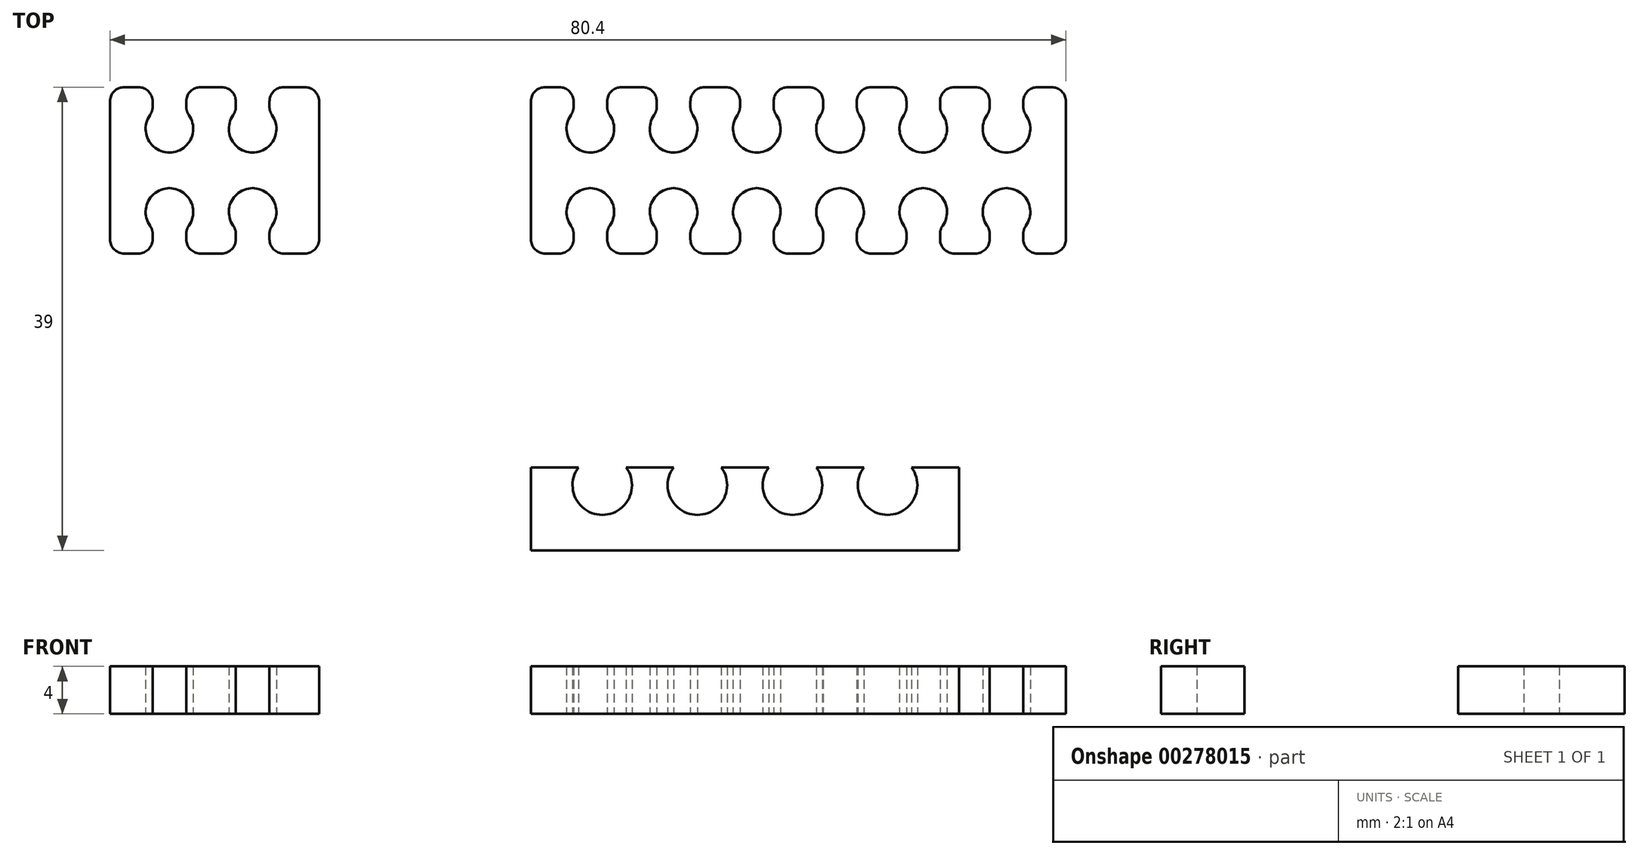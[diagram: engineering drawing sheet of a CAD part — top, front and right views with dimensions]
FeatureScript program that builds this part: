
annotation { "Feature Type Name" : "Feature", "Feature Type Description" : "" }
export const myFeature = defineFeature(function(context is Context, id is Id, definition is map)
    precondition{}
    {
        {
            var Q0;
            Q0=qCreatedBy(makeId("Top.planeOp"),FACE);
            var sketch = newSketch(context, id + "F0", { "sketchPlane" : qUnion([Q0])});
            skArc(sketch, "E0", {"start": v(4, 7) * mm, "mid": v(6, 3) * mm, "end": v(8, 7) * mm});
            skArc(sketch, "E1", {"start": v(12, 7) * mm, "mid": v(14, 3) * mm, "end": v(16, 7) * mm});
            skArc(sketch, "E2", {"start": v(20, 7) * mm, "mid": v(22, 3) * mm, "end": v(24, 7) * mm});
            skArc(sketch, "E3", {"start": v(28, 7) * mm, "mid": v(30, 3) * mm, "end": v(32, 7) * mm});
            skLineSegment(sketch, "E4", {"start": v(4, 7) * mm, "end": v(0, 7) * mm});
            skLineSegment(sketch, "E5", {"start": v(0, 7) * mm, "end": v(0, 0) * mm});
            skLineSegment(sketch, "E6", {"start": v(0, 0) * mm, "end": v(36, 0) * mm});
            skLineSegment(sketch, "E7", {"start": v(36, 0) * mm, "end": v(36, 7) * mm});
            skLineSegment(sketch, "E8", {"start": v(36, 7) * mm, "end": v(32, 7) * mm});
            skLineSegment(sketch, "E9", {"start": v(6, 5.5) * mm, "end": v(3.5, 5.5) * mm, "construction": true});
            skLineSegment(sketch, "E10", {"start": v(6, 5.5) * mm, "end": v(4, 7) * mm, "construction": true});
            skLineSegment(sketch, "E11", {"start": v(28, 7) * mm, "end": v(24, 7) * mm});
            skLineSegment(sketch, "E12", {"start": v(20, 7) * mm, "end": v(16, 7) * mm});
            skLineSegment(sketch, "E13", {"start": v(12, 7) * mm, "end": v(8, 7) * mm});
            skLineSegment(sketch, "E14", {"start": v(8.5, 5.5) * mm, "end": v(11.5, 5.5) * mm, "construction": true});
            skLineSegment(sketch, "E15", {"start": v(6, 3) * mm, "end": v(6, 0) * mm, "construction": true});
            skArc(sketch, "E16", {"start": v(3.37, 36.65) * mm, "mid": v(5, 33.5) * mm, "end": v(6.63, 36.65) * mm});
            skLineSegment(sketch, "E17", {"start": v(3.59, 37.35) * mm, "end": v(3.59, 37.8) * mm});
            skLineSegment(sketch, "E18", {"start": v(2.39, 39) * mm, "end": v(1.5, 39) * mm});
            skLineSegment(sketch, "E19", {"start": v(6.41, 37.35) * mm, "end": v(6.41, 37.8) * mm});
            skLineSegment(sketch, "E20", {"start": v(7.61, 39) * mm, "end": v(8.5, 39) * mm});
            skLineSegment(sketch, "E21", {"start": v(5, 35.5) * mm, "end": v(3, 35.5) * mm, "construction": true});
            skLineSegment(sketch, "E22", {"start": v(5, 35.5) * mm, "end": v(3.59, 36.91) * mm, "construction": true});
            skPoint(sketch, "E23.visualSharp", {"position": v(6.41, 36.91) * mm});
            skArc(sketch, "E23.filletArc", {"start": v(6.41, 37.35) * mm, "mid": v(6.47, 36.98) * mm, "end": v(6.63, 36.65) * mm});
            skPoint(sketch, "E24.visualSharp", {"position": v(6.41, 39) * mm});
            skArc(sketch, "E24.filletArc", {"start": v(7.61, 39) * mm, "mid": v(6.77, 38.65) * mm, "end": v(6.41, 37.8) * mm});
            skPoint(sketch, "E25.visualSharp", {"position": v(3.59, 39) * mm});
            skArc(sketch, "E25.filletArc", {"start": v(3.59, 37.8) * mm, "mid": v(3.23, 38.65) * mm, "end": v(2.39, 39) * mm});
            skPoint(sketch, "E26.visualSharp", {"position": v(3.59, 36.91) * mm});
            skArc(sketch, "E26.filletArc", {"start": v(3.37, 36.65) * mm, "mid": v(3.53, 36.98) * mm, "end": v(3.59, 37.35) * mm});
            skArc(sketch, "E27.1.0.0", {"start": v(10.37, 36.65) * mm, "mid": v(12, 33.5) * mm, "end": v(13.63, 36.65) * mm});
            skPoint(sketch, "E27.1.0.1", {"position": v(13.41, 36.91) * mm});
            skPoint(sketch, "E27.1.0.2", {"position": v(10.59, 36.91) * mm});
            skPoint(sketch, "E27.1.0.3", {"position": v(13.41, 39) * mm});
            skPoint(sketch, "E27.1.0.4", {"position": v(10.59, 39) * mm});
            skLineSegment(sketch, "E27.1.0.5", {"start": v(12, 35.5) * mm, "end": v(10, 35.5) * mm, "construction": true});
            skLineSegment(sketch, "E27.1.0.6", {"start": v(12, 35.5) * mm, "end": v(10.59, 36.91) * mm, "construction": true});
            skArc(sketch, "E27.1.0.7", {"start": v(10.59, 37.8) * mm, "mid": v(10.23, 38.65) * mm, "end": v(9.39, 39) * mm});
            skArc(sketch, "E27.1.0.8", {"start": v(14.61, 39) * mm, "mid": v(13.77, 38.65) * mm, "end": v(13.41, 37.8) * mm});
            skLineSegment(sketch, "E27.1.0.9", {"start": v(9.39, 39) * mm, "end": v(8.5, 39) * mm});
            skLineSegment(sketch, "E27.1.0.10", {"start": v(14.61, 39) * mm, "end": v(15.5, 39) * mm});
            skLineSegment(sketch, "E27.1.0.11", {"start": v(10.59, 37.35) * mm, "end": v(10.59, 37.8) * mm});
            skLineSegment(sketch, "E27.1.0.12", {"start": v(13.41, 37.35) * mm, "end": v(13.41, 37.8) * mm});
            skArc(sketch, "E27.1.0.13", {"start": v(10.37, 36.65) * mm, "mid": v(10.53, 36.98) * mm, "end": v(10.59, 37.35) * mm});
            skArc(sketch, "E27.1.0.14", {"start": v(13.41, 37.35) * mm, "mid": v(13.47, 36.98) * mm, "end": v(13.63, 36.65) * mm});
            skArc(sketch, "E27.2.0.0", {"start": v(17.37, 36.65) * mm, "mid": v(19, 33.5) * mm, "end": v(20.63, 36.65) * mm});
            skPoint(sketch, "E27.2.0.1", {"position": v(20.41, 36.91) * mm});
            skPoint(sketch, "E27.2.0.2", {"position": v(17.59, 36.91) * mm});
            skPoint(sketch, "E27.2.0.3", {"position": v(20.41, 39) * mm});
            skPoint(sketch, "E27.2.0.4", {"position": v(17.59, 39) * mm});
            skLineSegment(sketch, "E27.2.0.5", {"start": v(19, 35.5) * mm, "end": v(17, 35.5) * mm, "construction": true});
            skLineSegment(sketch, "E27.2.0.6", {"start": v(19, 35.5) * mm, "end": v(17.59, 36.91) * mm, "construction": true});
            skArc(sketch, "E27.2.0.7", {"start": v(17.59, 37.8) * mm, "mid": v(17.23, 38.65) * mm, "end": v(16.39, 39) * mm});
            skArc(sketch, "E27.2.0.8", {"start": v(21.61, 39) * mm, "mid": v(20.77, 38.65) * mm, "end": v(20.41, 37.8) * mm});
            skLineSegment(sketch, "E27.2.0.9", {"start": v(16.39, 39) * mm, "end": v(15.5, 39) * mm});
            skLineSegment(sketch, "E27.2.0.10", {"start": v(21.61, 39) * mm, "end": v(22.5, 39) * mm});
            skLineSegment(sketch, "E27.2.0.11", {"start": v(17.59, 37.35) * mm, "end": v(17.59, 37.8) * mm});
            skLineSegment(sketch, "E27.2.0.12", {"start": v(20.41, 37.35) * mm, "end": v(20.41, 37.8) * mm});
            skArc(sketch, "E27.2.0.13", {"start": v(17.37, 36.65) * mm, "mid": v(17.53, 36.98) * mm, "end": v(17.59, 37.35) * mm});
            skArc(sketch, "E27.2.0.14", {"start": v(20.41, 37.35) * mm, "mid": v(20.47, 36.98) * mm, "end": v(20.63, 36.65) * mm});
            skArc(sketch, "E27.3.0.0", {"start": v(24.37, 36.65) * mm, "mid": v(26, 33.5) * mm, "end": v(27.63, 36.65) * mm});
            skPoint(sketch, "E27.3.0.1", {"position": v(27.41, 36.91) * mm});
            skPoint(sketch, "E27.3.0.2", {"position": v(24.59, 36.91) * mm});
            skPoint(sketch, "E27.3.0.3", {"position": v(27.41, 39) * mm});
            skPoint(sketch, "E27.3.0.4", {"position": v(24.59, 39) * mm});
            skLineSegment(sketch, "E27.3.0.5", {"start": v(26, 35.5) * mm, "end": v(24, 35.5) * mm, "construction": true});
            skLineSegment(sketch, "E27.3.0.6", {"start": v(26, 35.5) * mm, "end": v(24.59, 36.91) * mm, "construction": true});
            skArc(sketch, "E27.3.0.7", {"start": v(24.59, 37.8) * mm, "mid": v(24.23, 38.65) * mm, "end": v(23.39, 39) * mm});
            skArc(sketch, "E27.3.0.8", {"start": v(28.61, 39) * mm, "mid": v(27.77, 38.65) * mm, "end": v(27.41, 37.8) * mm});
            skLineSegment(sketch, "E27.3.0.9", {"start": v(23.39, 39) * mm, "end": v(22.5, 39) * mm});
            skLineSegment(sketch, "E27.3.0.10", {"start": v(28.61, 39) * mm, "end": v(29.5, 39) * mm});
            skLineSegment(sketch, "E27.3.0.11", {"start": v(24.59, 37.35) * mm, "end": v(24.59, 37.8) * mm});
            skLineSegment(sketch, "E27.3.0.12", {"start": v(27.41, 37.35) * mm, "end": v(27.41, 37.8) * mm});
            skArc(sketch, "E27.3.0.13", {"start": v(24.37, 36.65) * mm, "mid": v(24.53, 36.98) * mm, "end": v(24.59, 37.35) * mm});
            skArc(sketch, "E27.3.0.14", {"start": v(27.41, 37.35) * mm, "mid": v(27.47, 36.98) * mm, "end": v(27.63, 36.65) * mm});
            skArc(sketch, "E27.4.0.0", {"start": v(31.37, 36.65) * mm, "mid": v(33, 33.5) * mm, "end": v(34.63, 36.65) * mm});
            skPoint(sketch, "E27.4.0.1", {"position": v(34.41, 36.91) * mm});
            skPoint(sketch, "E27.4.0.2", {"position": v(31.59, 36.91) * mm});
            skPoint(sketch, "E27.4.0.3", {"position": v(34.41, 39) * mm});
            skPoint(sketch, "E27.4.0.4", {"position": v(31.59, 39) * mm});
            skLineSegment(sketch, "E27.4.0.5", {"start": v(33, 35.5) * mm, "end": v(31, 35.5) * mm, "construction": true});
            skLineSegment(sketch, "E27.4.0.6", {"start": v(33, 35.5) * mm, "end": v(31.59, 36.91) * mm, "construction": true});
            skArc(sketch, "E27.4.0.7", {"start": v(31.59, 37.8) * mm, "mid": v(31.23, 38.65) * mm, "end": v(30.39, 39) * mm});
            skArc(sketch, "E27.4.0.8", {"start": v(35.61, 39) * mm, "mid": v(34.77, 38.65) * mm, "end": v(34.41, 37.8) * mm});
            skLineSegment(sketch, "E27.4.0.9", {"start": v(30.39, 39) * mm, "end": v(29.5, 39) * mm});
            skLineSegment(sketch, "E27.4.0.10", {"start": v(35.61, 39) * mm, "end": v(36.5, 39) * mm});
            skLineSegment(sketch, "E27.4.0.11", {"start": v(31.59, 37.35) * mm, "end": v(31.59, 37.8) * mm});
            skLineSegment(sketch, "E27.4.0.12", {"start": v(34.41, 37.35) * mm, "end": v(34.41, 37.8) * mm});
            skArc(sketch, "E27.4.0.13", {"start": v(31.37, 36.65) * mm, "mid": v(31.53, 36.98) * mm, "end": v(31.59, 37.35) * mm});
            skArc(sketch, "E27.4.0.14", {"start": v(34.41, 37.35) * mm, "mid": v(34.47, 36.98) * mm, "end": v(34.63, 36.65) * mm});
            skArc(sketch, "E27.5.0.0", {"start": v(38.37, 36.65) * mm, "mid": v(40, 33.5) * mm, "end": v(41.63, 36.65) * mm});
            skPoint(sketch, "E27.5.0.1", {"position": v(41.41, 36.91) * mm});
            skPoint(sketch, "E27.5.0.2", {"position": v(38.59, 36.91) * mm});
            skPoint(sketch, "E27.5.0.3", {"position": v(41.41, 39) * mm});
            skPoint(sketch, "E27.5.0.4", {"position": v(38.59, 39) * mm});
            skLineSegment(sketch, "E27.5.0.5", {"start": v(40, 35.5) * mm, "end": v(38, 35.5) * mm, "construction": true});
            skLineSegment(sketch, "E27.5.0.6", {"start": v(40, 35.5) * mm, "end": v(38.59, 36.91) * mm, "construction": true});
            skArc(sketch, "E27.5.0.7", {"start": v(38.59, 37.8) * mm, "mid": v(38.23, 38.65) * mm, "end": v(37.39, 39) * mm});
            skArc(sketch, "E27.5.0.8", {"start": v(42.61, 39) * mm, "mid": v(41.77, 38.65) * mm, "end": v(41.41, 37.8) * mm});
            skLineSegment(sketch, "E27.5.0.9", {"start": v(37.39, 39) * mm, "end": v(36.5, 39) * mm});
            skLineSegment(sketch, "E27.5.0.10", {"start": v(42.61, 39) * mm, "end": v(43.5, 39) * mm});
            skLineSegment(sketch, "E27.5.0.11", {"start": v(38.59, 37.35) * mm, "end": v(38.59, 37.8) * mm});
            skLineSegment(sketch, "E27.5.0.12", {"start": v(41.41, 37.35) * mm, "end": v(41.41, 37.8) * mm});
            skArc(sketch, "E27.5.0.13", {"start": v(38.37, 36.65) * mm, "mid": v(38.53, 36.98) * mm, "end": v(38.59, 37.35) * mm});
            skArc(sketch, "E27.5.0.14", {"start": v(41.41, 37.35) * mm, "mid": v(41.47, 36.98) * mm, "end": v(41.63, 36.65) * mm});
            skLineSegment(sketch, "E27.direction1", {"start": v(3, 35.5) * mm, "end": v(10, 35.5) * mm, "construction": true});
            skLineSegment(sketch, "E28", {"start": v(5, 32) * mm, "end": v(12, 32) * mm, "construction": true});
            skPoint(sketch, "E29", {"position": v(5, 33.5) * mm});
            skPoint(sketch, "E30", {"position": v(7, 35.5) * mm});
            skPoint(sketch, "E31", {"position": v(10, 35.5) * mm});
            skLineSegment(sketch, "E32.MirrorCS", {"start": v(24.59, 26.65) * mm, "end": v(24.59, 26.2) * mm});
            skLineSegment(sketch, "E33.MirrorCS", {"start": v(10.59, 26.65) * mm, "end": v(10.59, 26.2) * mm});
            skLineSegment(sketch, "E34.MirrorCS", {"start": v(27.41, 26.65) * mm, "end": v(27.41, 26.2) * mm});
            skArc(sketch, "E35.MirrorCS", {"start": v(41.41, 26.65) * mm, "mid": v(41.47, 27.02) * mm, "end": v(41.63, 27.35) * mm});
            skLineSegment(sketch, "E36.MirrorCS", {"start": v(3.59, 26.65) * mm, "end": v(3.59, 26.2) * mm});
            skArc(sketch, "E37.MirrorCS", {"start": v(20.41, 26.65) * mm, "mid": v(20.47, 27.02) * mm, "end": v(20.63, 27.35) * mm});
            skArc(sketch, "E38.MirrorCS", {"start": v(38.37, 27.35) * mm, "mid": v(38.53, 27.02) * mm, "end": v(38.59, 26.65) * mm});
            skArc(sketch, "E39.MirrorCS", {"start": v(6.41, 26.65) * mm, "mid": v(6.47, 27.02) * mm, "end": v(6.63, 27.35) * mm});
            skArc(sketch, "E40.MirrorCS", {"start": v(17.37, 27.35) * mm, "mid": v(17.53, 27.02) * mm, "end": v(17.59, 26.65) * mm});
            skArc(sketch, "E41.MirrorCS", {"start": v(34.41, 26.65) * mm, "mid": v(34.47, 27.02) * mm, "end": v(34.63, 27.35) * mm});
            skLineSegment(sketch, "E42.MirrorCS", {"start": v(41.41, 26.65) * mm, "end": v(41.41, 26.2) * mm});
            skArc(sketch, "E43.MirrorCS", {"start": v(3.37, 27.35) * mm, "mid": v(3.53, 27.02) * mm, "end": v(3.59, 26.65) * mm});
            skLineSegment(sketch, "E44.MirrorCS", {"start": v(34.41, 26.65) * mm, "end": v(34.41, 26.2) * mm});
            skArc(sketch, "E45.MirrorCS", {"start": v(27.41, 26.65) * mm, "mid": v(27.47, 27.02) * mm, "end": v(27.63, 27.35) * mm});
            skArc(sketch, "E46.MirrorCS", {"start": v(24.37, 27.35) * mm, "mid": v(24.53, 27.02) * mm, "end": v(24.59, 26.65) * mm});
            skLineSegment(sketch, "E47.MirrorCS", {"start": v(13.41, 26.65) * mm, "end": v(13.41, 26.2) * mm});
            skLineSegment(sketch, "E48.MirrorCS", {"start": v(38.59, 26.65) * mm, "end": v(38.59, 26.2) * mm});
            skLineSegment(sketch, "E49.MirrorCS", {"start": v(31.59, 26.65) * mm, "end": v(31.59, 26.2) * mm});
            skLineSegment(sketch, "E50.MirrorCS", {"start": v(6.41, 26.65) * mm, "end": v(6.41, 26.2) * mm});
            skLineSegment(sketch, "E51.MirrorCS", {"start": v(17.59, 26.65) * mm, "end": v(17.59, 26.2) * mm});
            skArc(sketch, "E52.MirrorCS", {"start": v(13.41, 26.65) * mm, "mid": v(13.47, 27.02) * mm, "end": v(13.63, 27.35) * mm});
            skLineSegment(sketch, "E53.MirrorCS", {"start": v(20.41, 26.65) * mm, "end": v(20.41, 26.2) * mm});
            skArc(sketch, "E54.MirrorCS", {"start": v(31.37, 27.35) * mm, "mid": v(31.53, 27.02) * mm, "end": v(31.59, 26.65) * mm});
            skArc(sketch, "E55.MirrorCS", {"start": v(10.37, 27.35) * mm, "mid": v(10.53, 27.02) * mm, "end": v(10.59, 26.65) * mm});
            skLineSegment(sketch, "E56.MirrorCS", {"start": v(35.61, 25) * mm, "end": v(36.5, 25) * mm});
            skLineSegment(sketch, "E57.MirrorCS", {"start": v(14.61, 25) * mm, "end": v(15.5, 25) * mm});
            skLineSegment(sketch, "E58.MirrorCS", {"start": v(30.39, 25) * mm, "end": v(29.5, 25) * mm});
            skLineSegment(sketch, "E59.MirrorCS", {"start": v(9.39, 25) * mm, "end": v(8.5, 25) * mm});
            skLineSegment(sketch, "E60.MirrorCS", {"start": v(28.61, 25) * mm, "end": v(29.5, 25) * mm});
            skLineSegment(sketch, "E61.MirrorCS", {"start": v(23.39, 25) * mm, "end": v(22.5, 25) * mm});
            skLineSegment(sketch, "E62.MirrorCS", {"start": v(16.39, 25) * mm, "end": v(15.5, 25) * mm});
            skLineSegment(sketch, "E63.MirrorCS", {"start": v(7.61, 25) * mm, "end": v(8.5, 25) * mm});
            skLineSegment(sketch, "E64.MirrorCS", {"start": v(37.39, 25) * mm, "end": v(36.5, 25) * mm});
            skLineSegment(sketch, "E65.MirrorCS", {"start": v(21.61, 25) * mm, "end": v(22.5, 25) * mm});
            skLineSegment(sketch, "E66.MirrorCS", {"start": v(2.39, 25) * mm, "end": v(1.5, 25) * mm});
            skArc(sketch, "E67.MirrorCS", {"start": v(17.59, 26.2) * mm, "mid": v(17.23, 25.35) * mm, "end": v(16.39, 25) * mm});
            skArc(sketch, "E68.MirrorCS", {"start": v(3.59, 26.2) * mm, "mid": v(3.23, 25.35) * mm, "end": v(2.39, 25) * mm});
            skArc(sketch, "E69.MirrorCS", {"start": v(7.61, 25) * mm, "mid": v(6.77, 25.35) * mm, "end": v(6.41, 26.2) * mm});
            skArc(sketch, "E70.MirrorCS", {"start": v(35.61, 25) * mm, "mid": v(34.77, 25.35) * mm, "end": v(34.41, 26.2) * mm});
            skArc(sketch, "E71.MirrorCS", {"start": v(14.61, 25) * mm, "mid": v(13.77, 25.35) * mm, "end": v(13.41, 26.2) * mm});
            skArc(sketch, "E72.MirrorCS", {"start": v(31.59, 26.2) * mm, "mid": v(31.23, 25.35) * mm, "end": v(30.39, 25) * mm});
            skArc(sketch, "E73.MirrorCS", {"start": v(21.61, 25) * mm, "mid": v(20.77, 25.35) * mm, "end": v(20.41, 26.2) * mm});
            skArc(sketch, "E74.MirrorCS", {"start": v(38.59, 26.2) * mm, "mid": v(38.23, 25.35) * mm, "end": v(37.39, 25) * mm});
            skArc(sketch, "E75.MirrorCS", {"start": v(42.61, 25) * mm, "mid": v(41.77, 25.35) * mm, "end": v(41.41, 26.2) * mm});
            skLineSegment(sketch, "E76.MirrorCS", {"start": v(42.61, 25) * mm, "end": v(43.5, 25) * mm});
            skLineSegment(sketch, "E77.MirrorCS", {"start": v(5, 28.5) * mm, "end": v(3, 28.5) * mm, "construction": true});
            skArc(sketch, "E78.MirrorCS", {"start": v(24.59, 26.2) * mm, "mid": v(24.23, 25.35) * mm, "end": v(23.39, 25) * mm});
            skArc(sketch, "E79.MirrorCS", {"start": v(10.59, 26.2) * mm, "mid": v(10.23, 25.35) * mm, "end": v(9.39, 25) * mm});
            skArc(sketch, "E80.MirrorCS", {"start": v(28.61, 25) * mm, "mid": v(27.77, 25.35) * mm, "end": v(27.41, 26.2) * mm});
            skPoint(sketch, "E81.MirrorP", {"position": v(10.59, 25) * mm});
            skPoint(sketch, "E82.MirrorP", {"position": v(24.59, 27.09) * mm});
            skLineSegment(sketch, "E83.MirrorCS", {"start": v(26, 28.5) * mm, "end": v(24, 28.5) * mm, "construction": true});
            skLineSegment(sketch, "E84.MirrorCS", {"start": v(3, 28.5) * mm, "end": v(10, 28.5) * mm, "construction": true});
            skPoint(sketch, "E85.MirrorP", {"position": v(31.59, 27.09) * mm});
            skPoint(sketch, "E86.MirrorP", {"position": v(5, 30.5) * mm});
            skLineSegment(sketch, "E87.MirrorCS", {"start": v(40, 28.5) * mm, "end": v(38.59, 27.09) * mm, "construction": true});
            skPoint(sketch, "E88.MirrorP", {"position": v(17.59, 25) * mm});
            skArc(sketch, "E89.MirrorCS", {"start": v(24.37, 27.35) * mm, "mid": v(26, 30.5) * mm, "end": v(27.63, 27.35) * mm});
            skPoint(sketch, "E90.MirrorP", {"position": v(34.41, 27.09) * mm});
            skPoint(sketch, "E91.MirrorP", {"position": v(3.59, 25) * mm});
            skPoint(sketch, "E92.MirrorP", {"position": v(20.41, 25) * mm});
            skLineSegment(sketch, "E93.MirrorCS", {"start": v(40, 28.5) * mm, "end": v(38, 28.5) * mm, "construction": true});
            skLineSegment(sketch, "E94.MirrorCS", {"start": v(19, 28.5) * mm, "end": v(17.59, 27.09) * mm, "construction": true});
            skPoint(sketch, "E95.MirrorP", {"position": v(13.41, 25) * mm});
            skPoint(sketch, "E96.MirrorP", {"position": v(27.41, 27.09) * mm});
            skArc(sketch, "E97.MirrorCS", {"start": v(3.37, 27.35) * mm, "mid": v(5, 30.5) * mm, "end": v(6.63, 27.35) * mm});
            skPoint(sketch, "E98.MirrorP", {"position": v(17.59, 27.09) * mm});
            skArc(sketch, "E99.MirrorCS", {"start": v(38.37, 27.35) * mm, "mid": v(40, 30.5) * mm, "end": v(41.63, 27.35) * mm});
            skLineSegment(sketch, "E100.MirrorCS", {"start": v(19, 28.5) * mm, "end": v(17, 28.5) * mm, "construction": true});
            skPoint(sketch, "E101.MirrorP", {"position": v(10.59, 27.09) * mm});
            skArc(sketch, "E102.MirrorCS", {"start": v(17.37, 27.35) * mm, "mid": v(19, 30.5) * mm, "end": v(20.63, 27.35) * mm});
            skLineSegment(sketch, "E103.MirrorCS", {"start": v(5, 28.5) * mm, "end": v(3.59, 27.09) * mm, "construction": true});
            skPoint(sketch, "E104.MirrorP", {"position": v(6.41, 25) * mm});
            skPoint(sketch, "E105.MirrorP", {"position": v(13.41, 27.09) * mm});
            skPoint(sketch, "E106.MirrorP", {"position": v(20.41, 27.09) * mm});
            skPoint(sketch, "E107.MirrorP", {"position": v(24.59, 25) * mm});
            skPoint(sketch, "E108.MirrorP", {"position": v(6.41, 27.09) * mm});
            skPoint(sketch, "E109.MirrorP", {"position": v(7, 28.5) * mm});
            skPoint(sketch, "E110.MirrorP", {"position": v(27.41, 25) * mm});
            skPoint(sketch, "E111.MirrorP", {"position": v(41.41, 27.09) * mm});
            skPoint(sketch, "E112.MirrorP", {"position": v(31.59, 25) * mm});
            skLineSegment(sketch, "E113.MirrorCS", {"start": v(26, 28.5) * mm, "end": v(24.59, 27.09) * mm, "construction": true});
            skPoint(sketch, "E114.MirrorP", {"position": v(10, 28.5) * mm});
            skPoint(sketch, "E115.MirrorP", {"position": v(38.59, 25) * mm});
            skArc(sketch, "E116.MirrorCS", {"start": v(10.37, 27.35) * mm, "mid": v(12, 30.5) * mm, "end": v(13.63, 27.35) * mm});
            skPoint(sketch, "E117.MirrorP", {"position": v(34.41, 25) * mm});
            skPoint(sketch, "E118.MirrorP", {"position": v(3.59, 27.09) * mm});
            skPoint(sketch, "E119.MirrorP", {"position": v(38.59, 27.09) * mm});
            skPoint(sketch, "E120.MirrorP", {"position": v(41.41, 25) * mm});
            skLineSegment(sketch, "E121.MirrorCS", {"start": v(33, 28.5) * mm, "end": v(31, 28.5) * mm, "construction": true});
            skLineSegment(sketch, "E122.MirrorCS", {"start": v(33, 28.5) * mm, "end": v(31.59, 27.09) * mm, "construction": true});
            skLineSegment(sketch, "E123.MirrorCS", {"start": v(12, 28.5) * mm, "end": v(10.59, 27.09) * mm, "construction": true});
            skLineSegment(sketch, "E124.MirrorCS", {"start": v(12, 28.5) * mm, "end": v(10, 28.5) * mm, "construction": true});
            skArc(sketch, "E125.MirrorCS", {"start": v(31.37, 27.35) * mm, "mid": v(33, 30.5) * mm, "end": v(34.63, 27.35) * mm});
            skLineSegment(sketch, "E126", {"start": v(1.5, 39) * mm, "end": v(1.2, 39) * mm});
            skLineSegment(sketch, "E127", {"start": v(0, 37.8) * mm, "end": v(0, 26.2) * mm});
            skLineSegment(sketch, "E128", {"start": v(1.2, 25) * mm, "end": v(1.5, 25) * mm});
            skLineSegment(sketch, "E129", {"start": v(43.5, 25) * mm, "end": v(43.8, 25) * mm});
            skLineSegment(sketch, "E130", {"start": v(45, 26.2) * mm, "end": v(45, 37.8) * mm});
            skLineSegment(sketch, "E131", {"start": v(43.8, 39) * mm, "end": v(43.5, 39) * mm});
            skPoint(sketch, "E132.visualSharp", {"position": v(0, 39) * mm});
            skArc(sketch, "E132.filletArc", {"start": v(1.2, 39) * mm, "mid": v(0.35, 38.65) * mm, "end": v(0, 37.8) * mm});
            skPoint(sketch, "E133.visualSharp", {"position": v(0, 25) * mm});
            skArc(sketch, "E133.filletArc", {"start": v(0, 26.2) * mm, "mid": v(0.35, 25.35) * mm, "end": v(1.2, 25) * mm});
            skPoint(sketch, "E134.visualSharp", {"position": v(45, 25) * mm});
            skArc(sketch, "E134.filletArc", {"start": v(43.8, 25) * mm, "mid": v(44.65, 25.35) * mm, "end": v(45, 26.2) * mm});
            skPoint(sketch, "E135.visualSharp", {"position": v(45, 39) * mm});
            skArc(sketch, "E135.filletArc", {"start": v(45, 37.8) * mm, "mid": v(44.65, 38.65) * mm, "end": v(43.8, 39) * mm});
            skLineSegment(sketch, "E136.1.0.0", {"start": v(-32.4, 35.5) * mm, "end": v(-25.4, 35.5) * mm, "construction": true});
            skPoint(sketch, "E136.1.0.1", {"position": v(-21.99, 39) * mm});
            skLineSegment(sketch, "E136.1.0.2", {"start": v(-23.4, 35.5) * mm, "end": v(-24.82, 36.91) * mm, "construction": true});
            skPoint(sketch, "E136.1.0.3", {"position": v(-31.82, 36.91) * mm});
            skPoint(sketch, "E136.1.0.4", {"position": v(-28.4, 35.5) * mm});
            skArc(sketch, "E136.1.0.5", {"start": v(-32.04, 27.35) * mm, "mid": v(-30.4, 30.5) * mm, "end": v(-28.77, 27.35) * mm});
            skLineSegment(sketch, "E136.1.0.6", {"start": v(-30.4, 28.5) * mm, "end": v(-32.4, 28.5) * mm, "construction": true});
            skArc(sketch, "E136.1.0.7", {"start": v(-25.04, 27.35) * mm, "mid": v(-23.4, 30.5) * mm, "end": v(-21.77, 27.35) * mm});
            skArc(sketch, "E136.1.0.8", {"start": v(-25.04, 36.65) * mm, "mid": v(-23.4, 33.5) * mm, "end": v(-21.77, 36.65) * mm});
            skPoint(sketch, "E136.1.0.9", {"position": v(-28.99, 27.09) * mm});
            skPoint(sketch, "E136.1.0.10", {"position": v(-24.82, 36.91) * mm});
            skPoint(sketch, "E136.1.0.11", {"position": v(-17.82, 25) * mm});
            skPoint(sketch, "E136.1.0.12", {"position": v(-35.4, 25) * mm});
            skPoint(sketch, "E136.1.0.13", {"position": v(-30.4, 30.5) * mm});
            skPoint(sketch, "E136.1.0.15", {"position": v(-25.4, 28.5) * mm});
            skArc(sketch, "E136.1.0.16", {"start": v(-32.04, 36.65) * mm, "mid": v(-30.4, 33.5) * mm, "end": v(-28.77, 36.65) * mm});
            skPoint(sketch, "E136.1.0.17", {"position": v(-21.99, 25) * mm});
            skPoint(sketch, "E136.1.0.18", {"position": v(-21.99, 36.91) * mm});
            skPoint(sketch, "E136.1.0.19", {"position": v(-28.99, 39) * mm});
            skLineSegment(sketch, "E136.1.0.20", {"start": v(-35.4, 37.8) * mm, "end": v(-35.4, 26.2) * mm});
            skPoint(sketch, "E136.1.0.21", {"position": v(-21.99, 27.09) * mm});
            skPoint(sketch, "E136.1.0.22", {"position": v(-35.4, 39) * mm});
            skPoint(sketch, "E136.1.0.23", {"position": v(-28.99, 25) * mm});
            skPoint(sketch, "E136.1.0.24", {"position": v(-24.82, 25) * mm});
            skPoint(sketch, "E136.1.0.25", {"position": v(-28.99, 36.91) * mm});
            skLineSegment(sketch, "E136.1.0.26", {"start": v(-32.4, 28.5) * mm, "end": v(-25.4, 28.5) * mm, "construction": true});
            skLineSegment(sketch, "E136.1.0.27", {"start": v(-30.4, 35.5) * mm, "end": v(-31.82, 36.91) * mm, "construction": true});
            skLineSegment(sketch, "E136.1.0.28", {"start": v(-23.4, 28.5) * mm, "end": v(-25.4, 28.5) * mm, "construction": true});
            skLineSegment(sketch, "E136.1.0.29", {"start": v(-30.4, 28.5) * mm, "end": v(-31.82, 27.09) * mm, "construction": true});
            skPoint(sketch, "E136.1.0.30", {"position": v(-24.82, 27.09) * mm});
            skPoint(sketch, "E136.1.0.31", {"position": v(-30.4, 33.5) * mm});
            skLineSegment(sketch, "E136.1.0.32", {"start": v(-23.4, 28.5) * mm, "end": v(-24.82, 27.09) * mm, "construction": true});
            skPoint(sketch, "E136.1.0.33", {"position": v(-31.82, 27.09) * mm});
            skPoint(sketch, "E136.1.0.34", {"position": v(-17.82, 39) * mm});
            skPoint(sketch, "E136.1.0.35", {"position": v(-31.82, 25) * mm});
            skLineSegment(sketch, "E136.1.0.36", {"start": v(-30.4, 32) * mm, "end": v(-23.4, 32) * mm, "construction": true});
            skLineSegment(sketch, "E136.1.0.37", {"start": v(-23.4, 35.5) * mm, "end": v(-25.4, 35.5) * mm, "construction": true});
            skPoint(sketch, "E136.1.0.38", {"position": v(-28.4, 28.5) * mm});
            skPoint(sketch, "E136.1.0.39", {"position": v(-25.4, 35.5) * mm});
            skPoint(sketch, "E136.1.0.41", {"position": v(-24.82, 39) * mm});
            skPoint(sketch, "E136.1.0.42", {"position": v(-31.82, 39) * mm});
            skArc(sketch, "E136.1.0.43", {"start": v(-34.2, 39) * mm, "mid": v(-35.05, 38.65) * mm, "end": v(-35.4, 37.8) * mm});
            skArc(sketch, "E136.1.0.44", {"start": v(-20.79, 25) * mm, "mid": v(-21.64, 25.35) * mm, "end": v(-21.99, 26.2) * mm});
            skArc(sketch, "E136.1.0.45", {"start": v(-27.79, 25) * mm, "mid": v(-28.64, 25.35) * mm, "end": v(-28.99, 26.2) * mm});
            skArc(sketch, "E136.1.0.46", {"start": v(-31.82, 37.8) * mm, "mid": v(-32.17, 38.65) * mm, "end": v(-33.02, 39) * mm});
            skArc(sketch, "E136.1.0.47", {"start": v(-17.82, 37.8) * mm, "mid": v(-18.17, 38.65) * mm, "end": v(-19.02, 39) * mm});
            skArc(sketch, "E136.1.0.48", {"start": v(-31.82, 26.2) * mm, "mid": v(-32.17, 25.35) * mm, "end": v(-33.02, 25) * mm});
            skArc(sketch, "E136.1.0.49", {"start": v(-27.79, 39) * mm, "mid": v(-28.64, 38.65) * mm, "end": v(-28.99, 37.8) * mm});
            skArc(sketch, "E136.1.0.50", {"start": v(-17.82, 26.2) * mm, "mid": v(-18.17, 25.35) * mm, "end": v(-19.02, 25) * mm});
            skArc(sketch, "E136.1.0.51", {"start": v(-20.79, 39) * mm, "mid": v(-21.64, 38.65) * mm, "end": v(-21.99, 37.8) * mm});
            skLineSegment(sketch, "E136.1.0.52", {"start": v(-30.4, 35.5) * mm, "end": v(-32.4, 35.5) * mm, "construction": true});
            skArc(sketch, "E136.1.0.53", {"start": v(-35.4, 26.2) * mm, "mid": v(-35.05, 25.35) * mm, "end": v(-34.2, 25) * mm});
            skArc(sketch, "E136.1.0.54", {"start": v(-24.82, 37.8) * mm, "mid": v(-25.17, 38.65) * mm, "end": v(-26.02, 39) * mm});
            skArc(sketch, "E136.1.0.55", {"start": v(-24.82, 26.2) * mm, "mid": v(-25.17, 25.35) * mm, "end": v(-26.02, 25) * mm});
            skLineSegment(sketch, "E136.1.0.56", {"start": v(-19.02, 25) * mm, "end": v(-19.9, 25) * mm});
            skLineSegment(sketch, "E136.1.0.57", {"start": v(-33.02, 39) * mm, "end": v(-33.9, 39) * mm});
            skLineSegment(sketch, "E136.1.0.58", {"start": v(-20.79, 25) * mm, "end": v(-19.9, 25) * mm});
            skArc(sketch, "E136.1.0.59", {"start": v(-28.99, 26.65) * mm, "mid": v(-28.93, 27.02) * mm, "end": v(-28.77, 27.35) * mm});
            skLineSegment(sketch, "E136.1.0.60", {"start": v(-20.79, 39) * mm, "end": v(-19.9, 39) * mm});
            skArc(sketch, "E136.1.0.61", {"start": v(-25.04, 27.35) * mm, "mid": v(-24.87, 27.02) * mm, "end": v(-24.82, 26.65) * mm});
            skLineSegment(sketch, "E136.1.0.62", {"start": v(-19.02, 39) * mm, "end": v(-19.9, 39) * mm});
            skLineSegment(sketch, "E136.1.0.63", {"start": v(-31.82, 37.35) * mm, "end": v(-31.82, 37.8) * mm});
            skArc(sketch, "E136.1.0.64", {"start": v(-32.04, 36.65) * mm, "mid": v(-31.87, 36.98) * mm, "end": v(-31.82, 37.35) * mm});
            skLineSegment(sketch, "E136.1.0.65", {"start": v(-26.02, 39) * mm, "end": v(-26.9, 39) * mm});
            skLineSegment(sketch, "E136.1.0.66", {"start": v(-34.2, 25) * mm, "end": v(-33.9, 25) * mm});
            skArc(sketch, "E136.1.0.67", {"start": v(-21.99, 26.65) * mm, "mid": v(-21.93, 27.02) * mm, "end": v(-21.77, 27.35) * mm});
            skLineSegment(sketch, "E136.1.0.68", {"start": v(-31.82, 26.65) * mm, "end": v(-31.82, 26.2) * mm});
            skLineSegment(sketch, "E136.1.0.69", {"start": v(-33.9, 39) * mm, "end": v(-34.2, 39) * mm});
            skArc(sketch, "E136.1.0.71", {"start": v(-28.99, 37.35) * mm, "mid": v(-28.93, 36.98) * mm, "end": v(-28.77, 36.65) * mm});
            skLineSegment(sketch, "E136.1.0.72", {"start": v(-28.99, 26.65) * mm, "end": v(-28.99, 26.2) * mm});
            skLineSegment(sketch, "E136.1.0.73", {"start": v(-26.02, 25) * mm, "end": v(-26.9, 25) * mm});
            skLineSegment(sketch, "E136.1.0.74", {"start": v(-33.02, 25) * mm, "end": v(-33.9, 25) * mm});
            skArc(sketch, "E136.1.0.75", {"start": v(-21.99, 37.35) * mm, "mid": v(-21.93, 36.98) * mm, "end": v(-21.77, 36.65) * mm});
            skLineSegment(sketch, "E136.1.0.77", {"start": v(-24.82, 26.65) * mm, "end": v(-24.82, 26.2) * mm});
            skArc(sketch, "E136.1.0.78", {"start": v(-25.04, 36.65) * mm, "mid": v(-24.87, 36.98) * mm, "end": v(-24.82, 37.35) * mm});
            skLineSegment(sketch, "E136.1.0.79", {"start": v(-27.79, 39) * mm, "end": v(-26.9, 39) * mm});
            skLineSegment(sketch, "E136.1.0.80", {"start": v(-21.99, 26.65) * mm, "end": v(-21.99, 26.2) * mm});
            skLineSegment(sketch, "E136.1.0.81", {"start": v(-27.79, 25) * mm, "end": v(-26.9, 25) * mm});
            skLineSegment(sketch, "E136.1.0.82", {"start": v(-24.82, 37.35) * mm, "end": v(-24.82, 37.8) * mm});
            skArc(sketch, "E136.1.0.84", {"start": v(-32.04, 27.35) * mm, "mid": v(-31.87, 27.02) * mm, "end": v(-31.82, 26.65) * mm});
            skLineSegment(sketch, "E136.1.0.85", {"start": v(-21.99, 37.35) * mm, "end": v(-21.99, 37.8) * mm});
            skLineSegment(sketch, "E136.1.0.87", {"start": v(-28.99, 37.35) * mm, "end": v(-28.99, 37.8) * mm});
            skLineSegment(sketch, "E136.direction1", {"start": v(0, 25) * mm, "end": v(-35.4, 25) * mm, "construction": true});
            skLineSegment(sketch, "E137", {"start": v(-17.82, 37.8) * mm, "end": v(-17.82, 26.2) * mm});
            skSolve(sketch);
        }
        {
            var Q0;
            Q0 = qSketchRegion(id + "F0", true);
            extrude(context, id + "F1", {"entities" : qUnion([Q0]), "depth" : 4 * mm});
        }
    });
